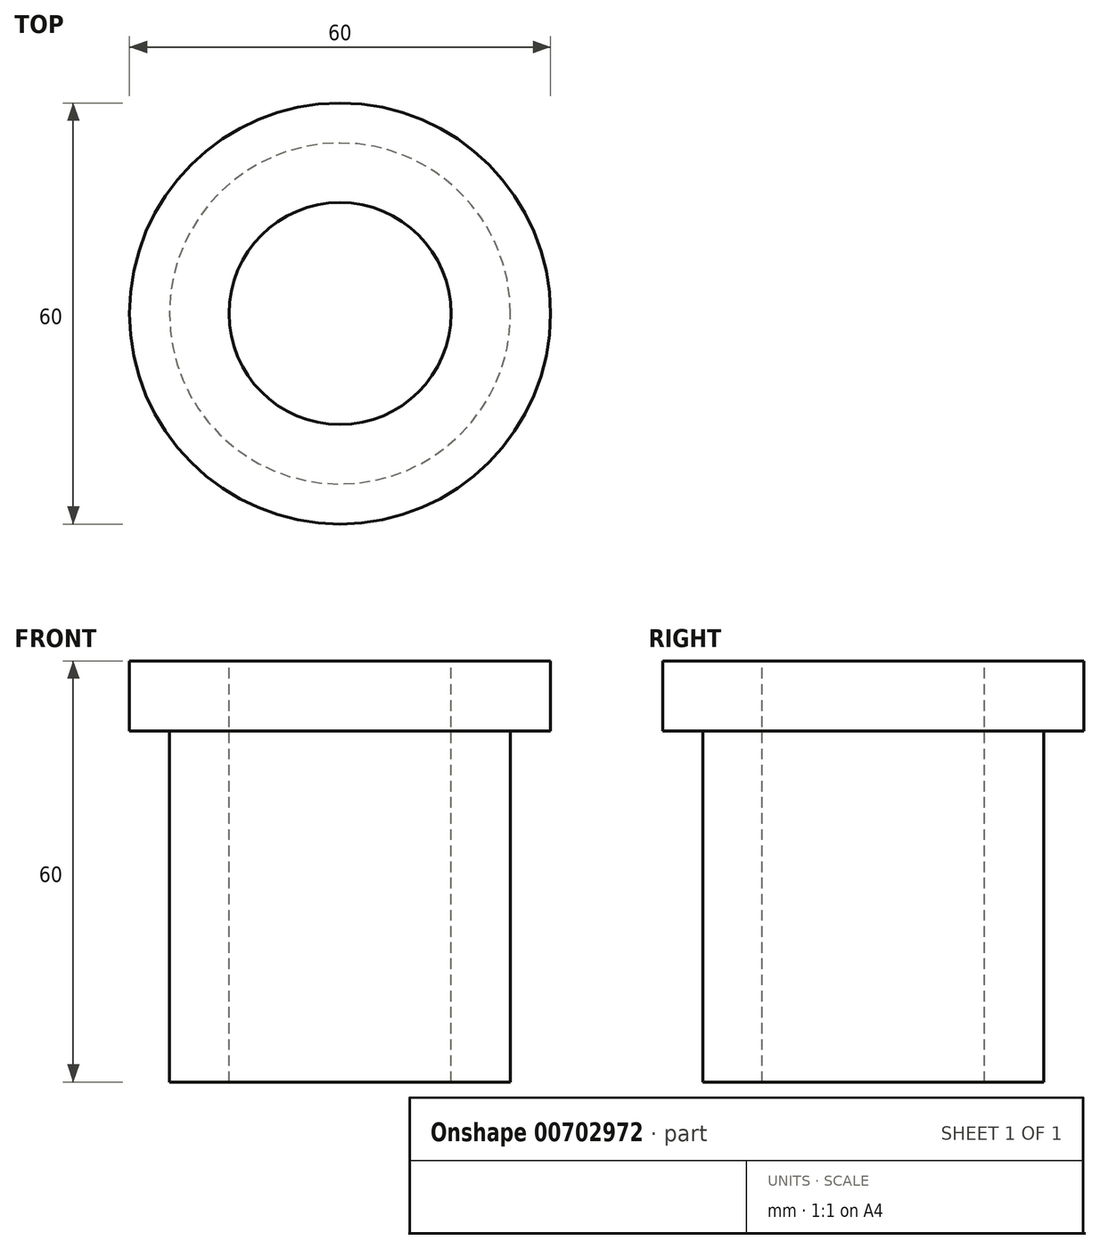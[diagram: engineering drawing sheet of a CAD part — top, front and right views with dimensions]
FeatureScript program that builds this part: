
annotation { "Feature Type Name" : "Feature", "Feature Type Description" : "" }
export const myFeature = defineFeature(function(context is Context, id is Id, definition is map)
    precondition{}
    {
        {
            var Q0;
            Q0=qCreatedBy(makeId("Front.planeOp"),FACE);
            var sketch = newSketch(context, id + "F0", { "sketchPlane" : qUnion([Q0])});
            skLineSegment(sketch, "E0", {"start": v(15.82, 60) * mm, "end": v(15.82, 0) * mm});
            skLineSegment(sketch, "E1", {"start": v(15.82, 60) * mm, "end": v(30, 60) * mm});
            skLineSegment(sketch, "E2", {"start": v(30, 60) * mm, "end": v(30, 50) * mm});
            skLineSegment(sketch, "E3", {"start": v(30, 50) * mm, "end": v(24.3, 50) * mm});
            skLineSegment(sketch, "E4", {"start": v(24.3, 50) * mm, "end": v(24.3, 0) * mm});
            skLineSegment(sketch, "E5", {"start": v(24.3, 0) * mm, "end": v(15.82, 0) * mm});
            skLineSegment(sketch, "E6", {"start": v(0, 68.36) * mm, "end": v(0, -23.84) * mm, "construction": true});
            skSolve(sketch);
        }
        {
            var Q0;
            Q0=makeQuery(id+"F0.imprint","IMPRINT",FACE,{"disambiguationData":[TD([[makeQuery(id+"F0.imprint","IMPRINT",EDGE,{"derivedFrom":sQuery(id+"F0.wireOp",EDGE,"E0")}),1.0]])]});
            var Q1;
            Q1=sQuery(id+"F0.wireOp",EDGE,"E6");
            revolve(context, id + "F1", {"surfaceOperationType" : NewSurfaceOperationType.NEW, "entities" : qUnion([Q0]), "axis" : qUnion([Q1]), "revolveType" : RevolveType.FULL});
        }
    });
